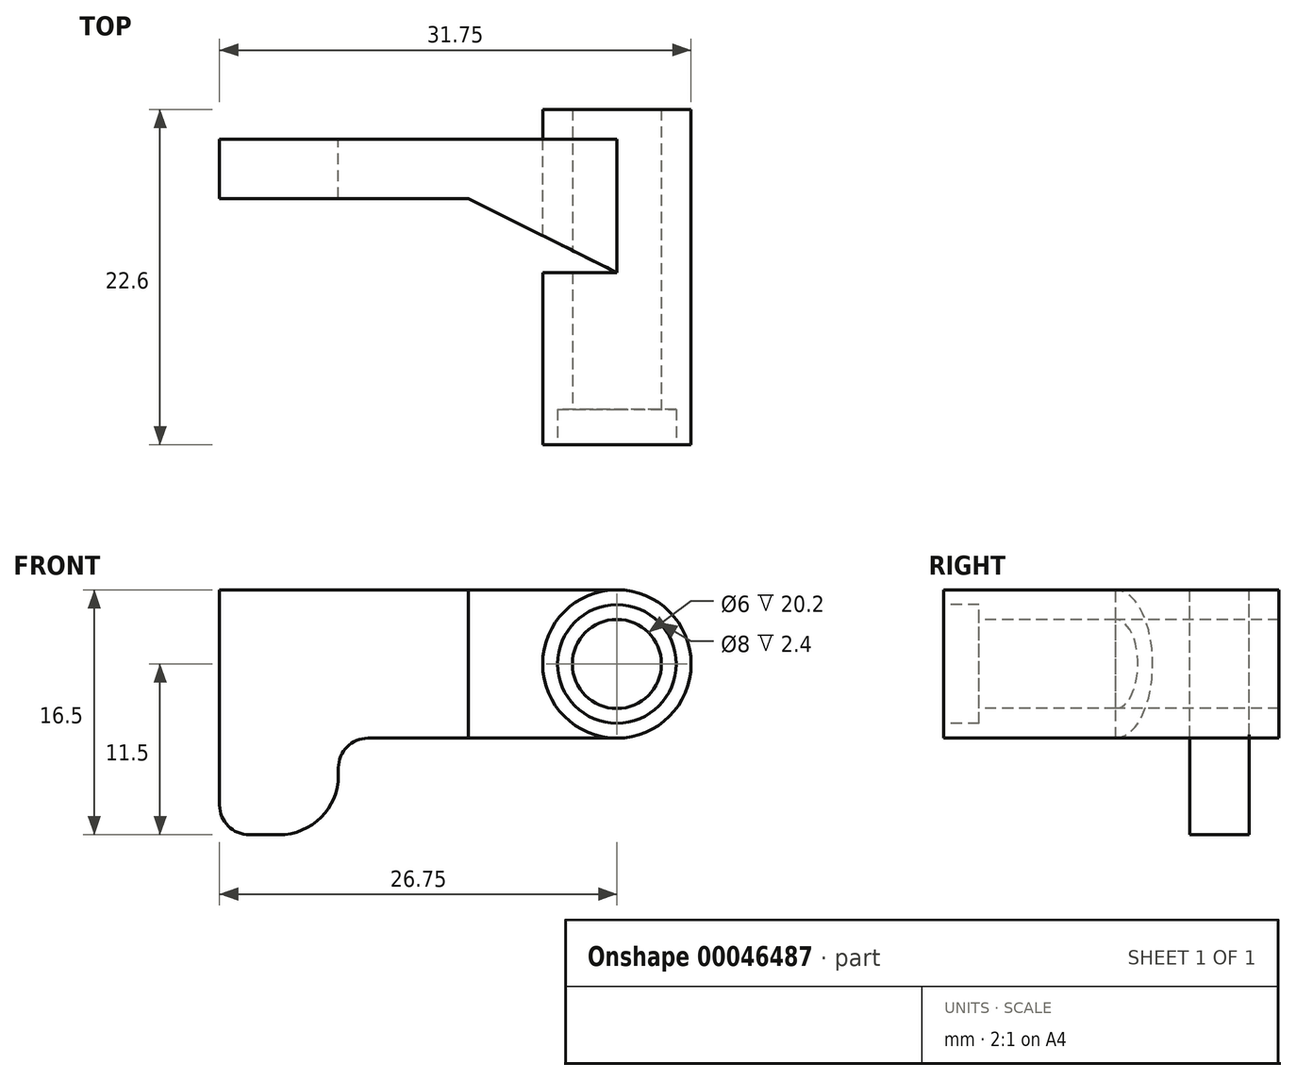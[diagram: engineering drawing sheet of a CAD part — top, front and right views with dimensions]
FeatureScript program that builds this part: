
annotation { "Feature Type Name" : "Feature", "Feature Type Description" : "" }
export const myFeature = defineFeature(function(context is Context, id is Id, definition is map)
    precondition{}
    {
        {
            var Q0;
            Q0=qCreatedBy(makeId("Front.planeOp"),FACE);
            var sketch = newSketch(context, id + "F0", { "sketchPlane" : qUnion([Q0])});
            skCircle(sketch, "E0", {"center": v(0, 0) * mm, "radius": 5 * mm});
            skSolve(sketch);
        }
        {
            var Q0;
            Q0=makeQuery(id+"F0.imprint","IMPRINT",FACE,{"disambiguationData":[TD([[makeQuery(id+"F0.imprint","IMPRINT",EDGE,{"derivedFrom":sQuery(id+"F0.wireOp",EDGE,"E0")}),1.0]])]});
            extrude(context, id + "F1", {"entities" : qUnion([Q0]), "depth" : 22.6 * mm});
        }
        {
            var Q0;
            Q0=makeQuery(id+"F1.opExtrude","CAP_FACE",FACE,{"disambiguationData":[OSD([sQuery(id+"F0.wireOp",EDGE,"E0")])],"isStart":false});
            var sketch = newSketch(context, id + "F2", { "sketchPlane" : qUnion([Q0])});
            skCircle(sketch, "E1", {"center": v(0, 0) * mm, "radius": 3 * mm});
            skSolve(sketch);
        }
        {
            var Q0;
            Q0=makeQuery(id+"F2.imprint","IMPRINT",FACE,{"disambiguationData":[TD([[makeQuery(id+"F2.imprint","IMPRINT",EDGE,{"derivedFrom":sQuery(id+"F2.wireOp",EDGE,"E1")}),1.0]])]});
            extrude(context, id + "F3", {"entities" : qUnion([Q0]), "operationType" : NewBodyOperationType.REMOVE, "oppositeDirection" : true, "depth" : 25 * mm});
        }
        {
            var Q0;
            Q0=makeQuery(id+"F1.opExtrude","CAP_FACE",FACE,{"disambiguationData":[OSD([sQuery(id+"F0.wireOp",EDGE,"E0")])],"isStart":false});
            var sketch = newSketch(context, id + "F4", { "sketchPlane" : qUnion([Q0])});
            skCircle(sketch, "E2", {"center": v(0, 0) * mm, "radius": 4 * mm});
            skSolve(sketch);
        }
        {
            var Q0;
            Q0=makeQuery(id+"F4.imprint","IMPRINT",FACE,{"disambiguationData":[TD([[makeQuery(id+"F4.imprint","IMPRINT",EDGE,{"derivedFrom":sQuery(id+"F4.wireOp",EDGE,"E2")}),1.0]])]});
            extrude(context, id + "F5", {"entities" : qUnion([Q0]), "operationType" : NewBodyOperationType.REMOVE, "oppositeDirection" : true, "depth" : 2.4 * mm});
        }
        {
            var Q0;
            Q0=makeQuery(id+"F1.opExtrude","CAP_FACE",FACE,{"disambiguationData":[OSD([sQuery(id+"F0.wireOp",EDGE,"E0")])],"isStart":true});
            cPlane(context, id + "F6", {"entities" : qUnion([Q0]), "cplaneType" : CPlaneType.OFFSET, "offset" : 2 * mm, "oppositeDirection" : true, "width" : 150 * mm, "height" : 150 * mm});
        }
        {
            var Q0;
            Q0=qCreatedBy(id+"F6.planeOp",FACE);
            var sketch = newSketch(context, id + "F7", { "sketchPlane" : qUnion([Q0])});
            skCircle(sketch, "E3.0", {"center": v(0, 0) * mm, "radius": 5 * mm, "construction": true});
            skLineSegment(sketch, "E4", {"start": v(0, 5) * mm, "end": v(26.02, 5) * mm, "construction": true});
            skLineSegment(sketch, "E5", {"start": v(0, -5) * mm, "end": v(27.86, -5) * mm, "construction": true});
            skLineSegment(sketch, "E6.bottom", {"start": v(0, -5) * mm, "end": v(26.75, -5) * mm});
            skLineSegment(sketch, "E6.top", {"start": v(0, 5) * mm, "end": v(26.75, 5) * mm});
            skLineSegment(sketch, "E6.left", {"start": v(0, -5) * mm, "end": v(0, 5) * mm});
            skLineSegment(sketch, "E6.right", {"start": v(26.75, -5) * mm, "end": v(26.75, 5) * mm});
            skArc(sketch, "E7", {"start": v(0, -5) * mm, "mid": v(5, 0) * mm, "end": v(0, 5) * mm});
            skLineSegment(sketch, "E8.bottom", {"start": v(26.75, 5) * mm, "end": v(18.75, 5) * mm});
            skLineSegment(sketch, "E8.top", {"start": v(26.75, -11.5) * mm, "end": v(18.75, -11.5) * mm});
            skLineSegment(sketch, "E8.left", {"start": v(26.75, 5) * mm, "end": v(26.75, -11.5) * mm});
            skLineSegment(sketch, "E8.right", {"start": v(18.75, 5) * mm, "end": v(18.75, -11.5) * mm});
            skSolve(sketch);
        }
        {
            var Q0;
            {var subQ3=sQuery(id+"F7.wireOp",EDGE,"E6.top");Q0=makeQuery(id+"F7.imprint","IMPRINT",FACE,{"disambiguationData":[TD([[makeQuery(id+"F7.imprint","IMPRINT",EDGE,{"derivedFrom":subQ3}),-1.0]])]});}
            var Q1;
            {var subQ3=sQuery(id+"F7.wireOp",EDGE,"E8.bottom");Q1=makeQuery(id+"F7.imprint","IMPRINT",FACE,{"disambiguationData":[TD([[makeQuery(id+"F7.imprint","IMPRINT",EDGE,{"derivedFrom":subQ3}),1.0]])]});}
            var Q2;
            {var subQ3=sQuery(id+"F7.wireOp",EDGE,"E8.top");Q2=makeQuery(id+"F7.imprint","IMPRINT",FACE,{"disambiguationData":[TD([[makeQuery(id+"F7.imprint","IMPRINT",EDGE,{"derivedFrom":subQ3}),-1.0]])]});}
            extrude(context, id + "F8", {"entities" : qUnion([Q0, Q1, Q2]), "oppositeDirection" : true, "depth" : 9 * mm});
        }
        {
            var Q0;
            Q0=makeQuery(id+"F8.opExtrude","SWEPT_FACE",FACE,{"disambiguationData":[OSD([sQuery(id+"F7.wireOp",EDGE,"E6.top"),sQuery(id+"F7.wireOp",EDGE,"E8.bottom")])]});
            var sketch = newSketch(context, id + "F9", { "sketchPlane" : qUnion([Q0])});
            skLineSegment(sketch, "E9", {"start": v(-5, -22.6) * mm, "end": v(-5, 0) * mm, "construction": true});
            skLineSegment(sketch, "E10.0", {"start": v(0, -11) * mm, "end": v(-26.75, -11) * mm, "construction": true});
            skLineSegment(sketch, "E11", {"start": v(8.5, -6) * mm, "end": v(-30.99, -6) * mm, "construction": true});
            skLineSegment(sketch, "E12", {"start": v(-5, -11) * mm, "end": v(-10, -6) * mm});
            skLineSegment(sketch, "E13", {"start": v(-10, -6) * mm, "end": v(-26.75, -6) * mm});
            skLineSegment(sketch, "E14", {"start": v(-26.75, -6) * mm, "end": v(-26.75, -11) * mm});
            skLineSegment(sketch, "E15", {"start": v(0, -11) * mm, "end": v(-10, -6) * mm});
            skSolve(sketch);
        }
        {
            var Q0;
            {var subQ2=sQuery(id+"F9.wireOp",EDGE,"E12");Q0=makeQuery(id+"F9.imprint","IMPRINT",FACE,{"disambiguationData":[TD([[makeQuery(id+"F9.imprint","IMPRINT",EDGE,{"derivedFrom":subQ2}),1.0]])]});}
            var Q1;
            {var subQ2=sQuery(id+"F9.wireOp",EDGE,"E12");Q1=makeQuery(id+"F9.imprint","IMPRINT",FACE,{"disambiguationData":[TD([[makeQuery(id+"F9.imprint","IMPRINT",EDGE,{"derivedFrom":subQ2}),-1.0]])]});}
            extrude(context, id + "F10", {"entities" : qUnion([Q0, Q1]), "operationType" : NewBodyOperationType.REMOVE, "oppositeDirection" : true, "depth" : 25 * mm});
        }
        {
            var Q0;
            Q0=makeQuery(id+"F8.opExtrude","SWEPT_EDGE",EDGE,{"disambiguationData":[OSD([sQuery(id+"F7.wireOp",EDGE,"E8.bottom"),sQuery(id+"F7.wireOp",EDGE,"E8.left")])]});
            fillet(context, id + "F11", {"entities" : qUnion([Q0]), "radius" : 2 * mm, "tangentPropagation" : true, "allowEdgeOverflow" : false});
        }
        {
            var Q0;
            Q0=makeQuery(id+"F8.opExtrude","SWEPT_EDGE",EDGE,{"disambiguationData":[OSD([sQuery(id+"F7.wireOp",EDGE,"E6.bottom"),sQuery(id+"F7.wireOp",EDGE,"E8.right")])]});
            fillet(context, id + "F12", {"entities" : qUnion([Q0]), "radius" : 2 * mm, "tangentPropagation" : true, "allowEdgeOverflow" : false});
        }
        {
            var Q0;
            Q0=makeQuery(id+"F8.opExtrude","SWEPT_EDGE",EDGE,{"disambiguationData":[OSD([sQuery(id+"F7.wireOp",EDGE,"E8.top"),sQuery(id+"F7.wireOp",EDGE,"E8.right")])]});
            var Q1;
            Q1=makeQuery(id+"F8.opExtrude","SWEPT_EDGE",EDGE,{"disambiguationData":[OSD([sQuery(id+"F7.wireOp",EDGE,"E8.top"),sQuery(id+"F7.wireOp",EDGE,"E8.left")])]});
            fillet(context, id + "F13", {"entities" : qUnion([Q0, Q1]), "radius" : 4 * mm, "tangentPropagation" : true, "allowEdgeOverflow" : false});
        }
    });
